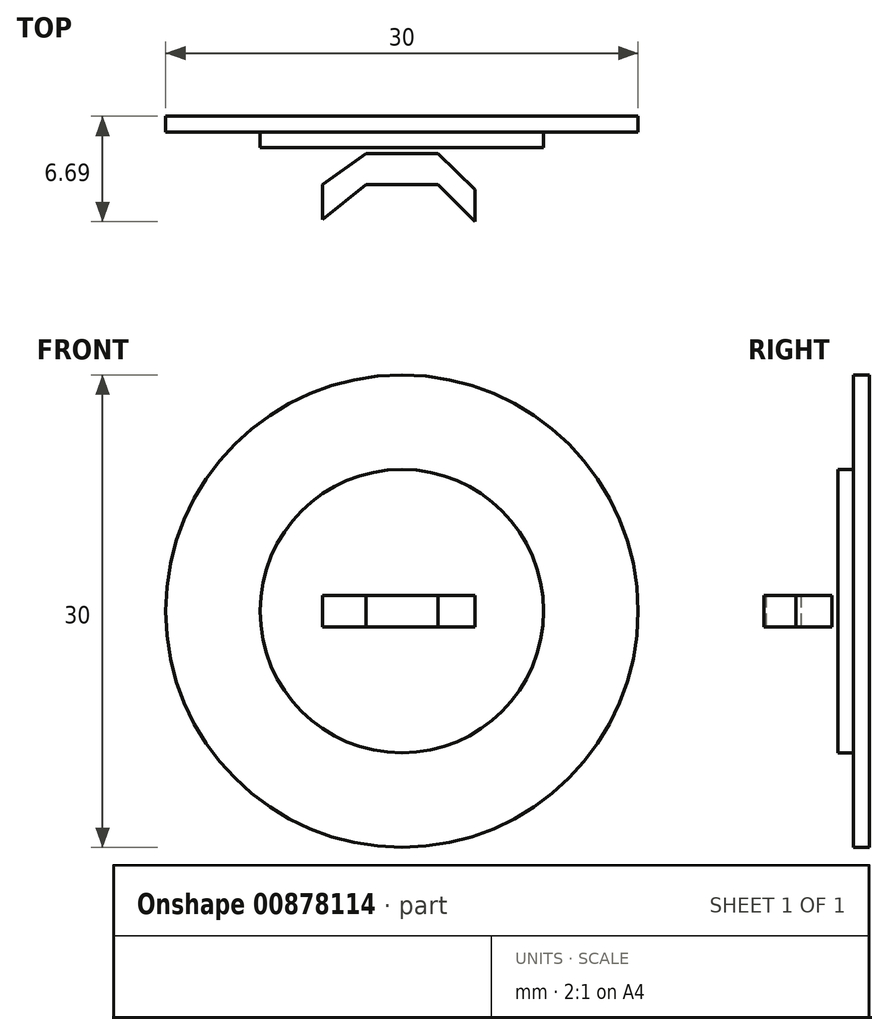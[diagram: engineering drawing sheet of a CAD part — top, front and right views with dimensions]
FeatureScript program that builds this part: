
annotation { "Feature Type Name" : "Feature", "Feature Type Description" : "" }
export const myFeature = defineFeature(function(context is Context, id is Id, definition is map)
    precondition{}
    {
        {
            var Q0;
            Q0=qCreatedBy(makeId("Front.planeOp"),FACE);
            var sketch = newSketch(context, id + "F0", { "sketchPlane" : qUnion([Q0])});
            skCircle(sketch, "E0", {"center": v(0, 0) * mm, "radius": 15 * mm});
            skSolve(sketch);
        }
        {
            var Q0;
            Q0=makeQuery(id+"F0.imprint","IMPRINT",FACE,{"disambiguationData":[TD([[makeQuery(id+"F0.imprint","IMPRINT",EDGE,{"derivedFrom":sQuery(id+"F0.wireOp",EDGE,"E0")}),1.0]])]});
            extrude(context, id + "F1", {"entities" : qUnion([Q0]), "depth" : 1 * mm, "offsetDistance" : 25 * mm});
        }
        {
            var Q0;
            Q0=makeQuery(id+"F1.opExtrude","CAP_FACE",FACE,{"disambiguationData":[OSD([sQuery(id+"F0.wireOp",EDGE,"E0")])],"isStart":false});
            var sketch = newSketch(context, id + "F2", { "sketchPlane" : qUnion([Q0])});
            skCircle(sketch, "E1", {"center": v(0, 0) * mm, "radius": 9 * mm});
            skSolve(sketch);
        }
        {
            var Q0;
            Q0=makeQuery(id+"F2.imprint","IMPRINT",FACE,{"disambiguationData":[TD([[makeQuery(id+"F2.imprint","IMPRINT",EDGE,{"derivedFrom":sQuery(id+"F2.wireOp",EDGE,"E1")}),1.0]])]});
            extrude(context, id + "F3", {"entities" : qUnion([Q0]), "depth" : 1 * mm, "offsetDistance" : 25 * mm});
        }
        {
            var Q0;
            Q0=qCreatedBy(makeId("Top.planeOp"),FACE);
            var sketch = newSketch(context, id + "F4", { "sketchPlane" : qUnion([Q0])});
            skLineSegment(sketch, "E2.bottom", {"start": v(-2.29, -4.34) * mm, "end": v(2.29, -4.34) * mm});
            skLineSegment(sketch, "E2.top", {"start": v(-2.29, -2.4) * mm, "end": v(2.29, -2.4) * mm});
            skLineSegment(sketch, "E2.left", {"start": v(-2.29, -4.34) * mm, "end": v(-2.29, -2.4) * mm});
            skLineSegment(sketch, "E2.right", {"start": v(2.29, -4.34) * mm, "end": v(2.29, -2.4) * mm});
            skPoint(sketch, "E2.middle", {"position": v(0, -3.36) * mm});
            skLineSegment(sketch, "E3", {"start": v(-2.29, -4.34) * mm, "end": v(-5.04, -6.57) * mm});
            skLineSegment(sketch, "E4", {"start": v(-5.04, -6.57) * mm, "end": v(-5.04, -4.34) * mm});
            skLineSegment(sketch, "E5", {"start": v(-5.04, -4.34) * mm, "end": v(-2.29, -2.4) * mm});
            skLineSegment(sketch, "E6", {"start": v(2.29, -4.34) * mm, "end": v(4.64, -6.69) * mm});
            skLineSegment(sketch, "E7", {"start": v(4.64, -6.69) * mm, "end": v(4.64, -4.66) * mm});
            skLineSegment(sketch, "E8", {"start": v(4.64, -4.66) * mm, "end": v(2.29, -2.4) * mm});
            skSolve(sketch);
        }
        {
            var Q0;
            Q0=makeQuery(id+"F4.imprint","IMPRINT",FACE,{"disambiguationData":[TD([[makeQuery(id+"F4.imprint","IMPRINT",EDGE,{"derivedFrom":sQuery(id+"F4.wireOp",EDGE,"E2.right")}),-1.0]])]});
            var Q1;
            Q1=makeQuery(id+"F4.imprint","IMPRINT",FACE,{"disambiguationData":[TD([[makeQuery(id+"F4.imprint","IMPRINT",EDGE,{"derivedFrom":sQuery(id+"F4.wireOp",EDGE,"E2.bottom")}),1.0]])]});
            var Q2;
            Q2=makeQuery(id+"F4.imprint","IMPRINT",FACE,{"disambiguationData":[TD([[makeQuery(id+"F4.imprint","IMPRINT",EDGE,{"derivedFrom":sQuery(id+"F4.wireOp",EDGE,"E2.left")}),1.0]])]});
            extrude(context, id + "F5", {"entities" : qUnion([Q0, Q1, Q2]), "depth" : 1 * mm, "offsetDistance" : 25 * mm});
        }
        {
            var Q0;
            Q0=makeQuery(id+"F5.opExtrude","CAP_FACE",FACE,{"disambiguationData":[OSD([sQuery(id+"F4.wireOp",EDGE,"E2.bottom"),sQuery(id+"F4.wireOp",EDGE,"E2.top"),sQuery(id+"F4.wireOp",EDGE,"E3"),sQuery(id+"F4.wireOp",EDGE,"E4"),sQuery(id+"F4.wireOp",EDGE,"E5"),sQuery(id+"F4.wireOp",EDGE,"E6"),sQuery(id+"F4.wireOp",EDGE,"E7"),sQuery(id+"F4.wireOp",EDGE,"E8")])],"isStart":true});
            extrude(context, id + "F6", {"entities" : qUnion([Q0]), "operationType" : NewBodyOperationType.ADD, "depth" : 1 * mm, "offsetDistance" : 25 * mm});
        }
    });
